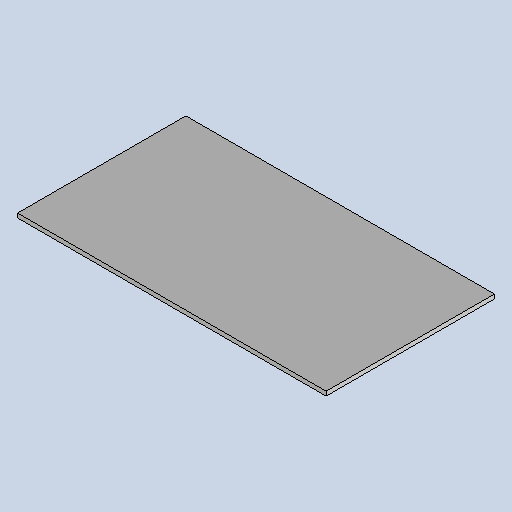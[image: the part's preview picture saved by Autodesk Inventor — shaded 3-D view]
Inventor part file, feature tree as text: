
AUTODESK INVENTOR PART (.ipt)
format: ipt  version: 2025.1 (Build 291241020, 241B)  size: 94,208 bytes
history: native  units: mm
features: sheet_metal_op x1, sketch x1, other x1
ambient origin geometry x8: Origin, YZ Plane, XZ Plane, XY Plane, X Axis, Y Axis, Z Axis, Center Point
bodies: Body1 (feature_tree)
feature tree (3):
  sheet_metal_op  "Face2"
  sketch  "Sketch4"  dims[d12=120.0mm d13=220.0mm d14=3.048mm]
  other  "Plate2"
